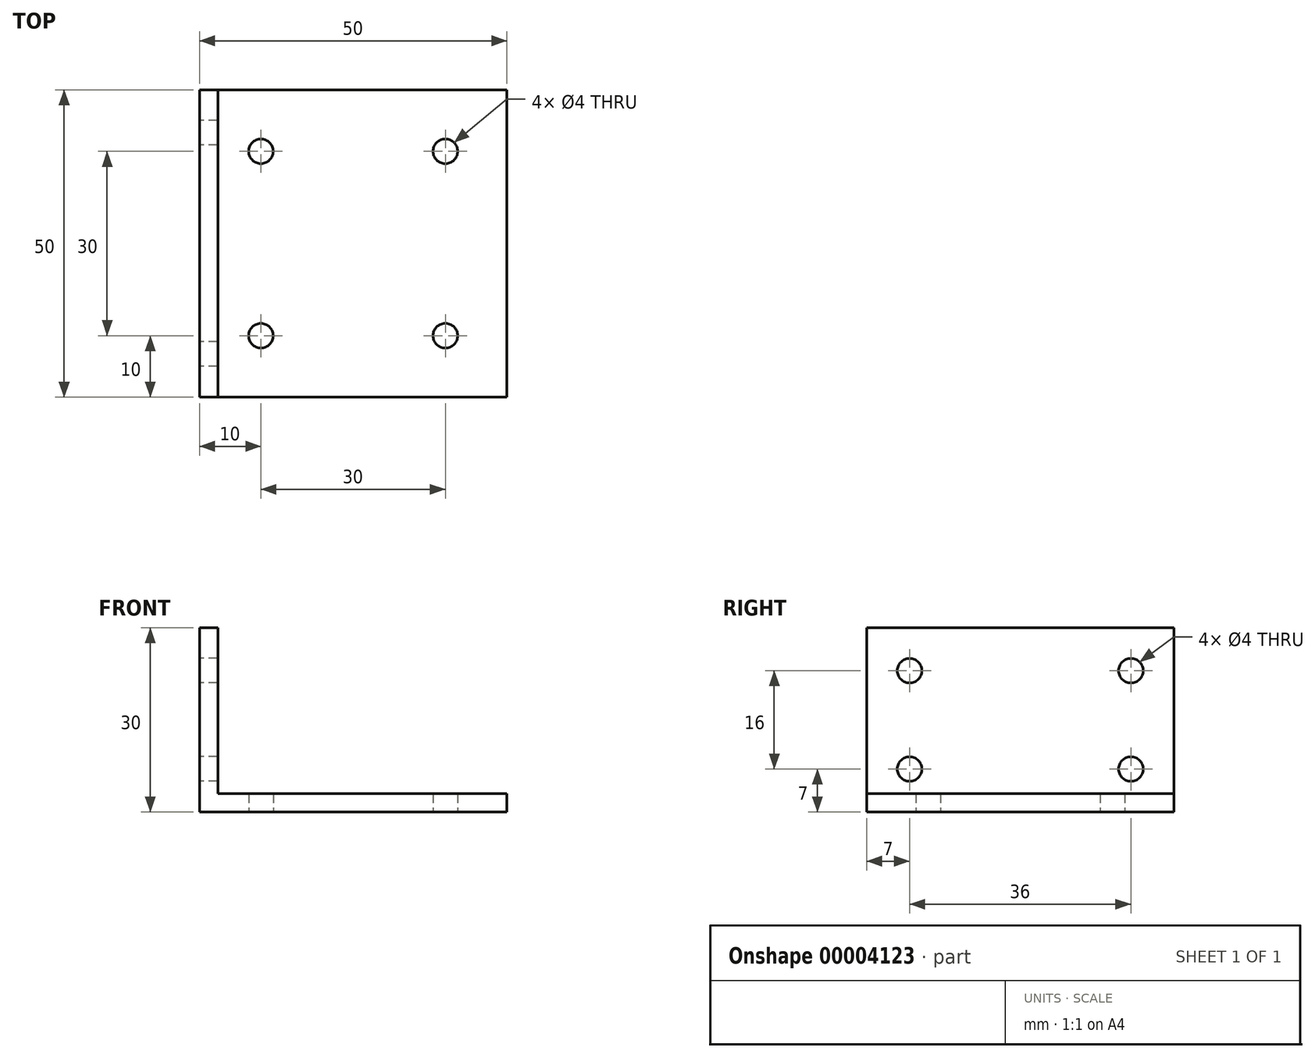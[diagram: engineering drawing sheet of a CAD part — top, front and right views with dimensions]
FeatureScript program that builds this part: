
annotation { "Feature Type Name" : "Feature", "Feature Type Description" : "" }
export const myFeature = defineFeature(function(context is Context, id is Id, definition is map)
    precondition{}
    {
        {
            var Q0;
            Q0=qCreatedBy(makeId("Front.planeOp"),FACE);
            var sketch = newSketch(context, id + "F0", { "sketchPlane" : qUnion([Q0])});
            skLineSegment(sketch, "E0", {"start": v(0, 0) * mm, "end": v(0, 30) * mm});
            skLineSegment(sketch, "E1", {"start": v(0, 30) * mm, "end": v(3, 30) * mm});
            skLineSegment(sketch, "E2", {"start": v(3, 30) * mm, "end": v(3, 3) * mm});
            skLineSegment(sketch, "E3", {"start": v(3, 3) * mm, "end": v(50, 3) * mm});
            skLineSegment(sketch, "E4", {"start": v(50, 3) * mm, "end": v(50, 0) * mm});
            skLineSegment(sketch, "E5", {"start": v(50, 0) * mm, "end": v(0, 0) * mm});
            skSolve(sketch);
        }
        {
            var Q0;
            Q0=makeQuery(id+"F0.imprint","IMPRINT",FACE,{"disambiguationData":[TD([[makeQuery(id+"F0.imprint","IMPRINT",EDGE,{"derivedFrom":sQuery(id+"F0.wireOp",EDGE,"E0")}),-1.0]])]});
            extrude(context, id + "F1", {"entities" : qUnion([Q0]), "depth" : 50 * mm});
        }
        {
            var Q0;
            Q0=makeQuery(id+"F1.opExtrude","SWEPT_FACE",FACE,{"disambiguationData":[OSD([sQuery(id+"F0.wireOp",EDGE,"E0")])]});
            var sketch = newSketch(context, id + "F2", { "sketchPlane" : qUnion([Q0])});
            skLineSegment(sketch, "E6.bottom", {"start": v(7, 23) * mm, "end": v(43, 23) * mm});
            skLineSegment(sketch, "E6.top", {"start": v(7, 7) * mm, "end": v(43, 7) * mm});
            skLineSegment(sketch, "E6.left", {"start": v(7, 23) * mm, "end": v(7, 7) * mm});
            skLineSegment(sketch, "E6.right", {"start": v(43, 23) * mm, "end": v(43, 7) * mm});
            skCircle(sketch, "E7", {"center": v(7, 23) * mm, "radius": 2 * mm});
            skCircle(sketch, "E8", {"center": v(43, 23) * mm, "radius": 2 * mm});
            skCircle(sketch, "E9", {"center": v(43, 7) * mm, "radius": 2 * mm});
            skCircle(sketch, "E10", {"center": v(7, 7) * mm, "radius": 2 * mm});
            skSolve(sketch);
        }
        {
            var Q0;
            {var subQ1=sQuery(id+"F2.wireOp",EDGE,"E6.left");var subQ3=sQuery(id+"F2.wireOp",EDGE,"E6.bottom");var subQ5=makeQuery(id+"F2.imprint","INTERSECT",VERTEX,{"derivedFrom":[subQ3,subQ1]});Q0=makeQuery(id+"F2.imprint","IMPRINT",FACE,{"disambiguationData":[TD([[makeQuery(id+"F2.imprint","IMPRINT",EDGE,{"disambiguationData":[TD([[subQ5,-1.0]])],"derivedFrom":subQ3}),1.0]])]});}
            var Q1;
            {var subQ1=sQuery(id+"F2.wireOp",EDGE,"E6.left");var subQ3=sQuery(id+"F2.wireOp",EDGE,"E6.bottom");var subQ5=makeQuery(id+"F2.imprint","INTERSECT",VERTEX,{"derivedFrom":[subQ3,subQ1]});Q1=makeQuery(id+"F2.imprint","IMPRINT",FACE,{"disambiguationData":[TD([[makeQuery(id+"F2.imprint","IMPRINT",EDGE,{"disambiguationData":[TD([[subQ5,-1.0]])],"derivedFrom":subQ3}),-1.0]])]});}
            var Q2;
            {var subQ1=sQuery(id+"F2.wireOp",EDGE,"E6.left");var subQ3=sQuery(id+"F2.wireOp",EDGE,"E6.top");var subQ5=makeQuery(id+"F2.imprint","INTERSECT",VERTEX,{"derivedFrom":[subQ3,subQ1]});Q2=makeQuery(id+"F2.imprint","IMPRINT",FACE,{"disambiguationData":[TD([[makeQuery(id+"F2.imprint","IMPRINT",EDGE,{"disambiguationData":[TD([[subQ5,-1.0]])],"derivedFrom":subQ3}),-1.0]])]});}
            var Q3;
            {var subQ1=sQuery(id+"F2.wireOp",EDGE,"E6.left");var subQ3=sQuery(id+"F2.wireOp",EDGE,"E6.top");var subQ5=makeQuery(id+"F2.imprint","INTERSECT",VERTEX,{"derivedFrom":[subQ3,subQ1]});Q3=makeQuery(id+"F2.imprint","IMPRINT",FACE,{"disambiguationData":[TD([[makeQuery(id+"F2.imprint","IMPRINT",EDGE,{"disambiguationData":[TD([[subQ5,-1.0]])],"derivedFrom":subQ3}),1.0]])]});}
            var Q4;
            {var subQ1=sQuery(id+"F2.wireOp",EDGE,"E6.right");var subQ3=sQuery(id+"F2.wireOp",EDGE,"E6.top");var subQ5=makeQuery(id+"F2.imprint","INTERSECT",VERTEX,{"derivedFrom":[subQ3,subQ1]});Q4=makeQuery(id+"F2.imprint","IMPRINT",FACE,{"disambiguationData":[TD([[makeQuery(id+"F2.imprint","IMPRINT",EDGE,{"disambiguationData":[TD([[subQ5,1.0]])],"derivedFrom":subQ3}),-1.0]])]});}
            var Q5;
            {var subQ1=sQuery(id+"F2.wireOp",EDGE,"E6.right");var subQ3=sQuery(id+"F2.wireOp",EDGE,"E6.top");var subQ5=makeQuery(id+"F2.imprint","INTERSECT",VERTEX,{"derivedFrom":[subQ3,subQ1]});Q5=makeQuery(id+"F2.imprint","IMPRINT",FACE,{"disambiguationData":[TD([[makeQuery(id+"F2.imprint","IMPRINT",EDGE,{"disambiguationData":[TD([[subQ5,1.0]])],"derivedFrom":subQ3}),1.0]])]});}
            var Q6;
            {var subQ1=sQuery(id+"F2.wireOp",EDGE,"E6.right");var subQ3=sQuery(id+"F2.wireOp",EDGE,"E6.bottom");var subQ5=makeQuery(id+"F2.imprint","INTERSECT",VERTEX,{"derivedFrom":[subQ3,subQ1]});Q6=makeQuery(id+"F2.imprint","IMPRINT",FACE,{"disambiguationData":[TD([[makeQuery(id+"F2.imprint","IMPRINT",EDGE,{"disambiguationData":[TD([[subQ5,1.0]])],"derivedFrom":subQ3}),1.0]])]});}
            var Q7;
            {var subQ1=sQuery(id+"F2.wireOp",EDGE,"E6.right");var subQ3=sQuery(id+"F2.wireOp",EDGE,"E6.bottom");var subQ5=makeQuery(id+"F2.imprint","INTERSECT",VERTEX,{"derivedFrom":[subQ3,subQ1]});Q7=makeQuery(id+"F2.imprint","IMPRINT",FACE,{"disambiguationData":[TD([[makeQuery(id+"F2.imprint","IMPRINT",EDGE,{"disambiguationData":[TD([[subQ5,1.0]])],"derivedFrom":subQ3}),-1.0]])]});}
            extrude(context, id + "F3", {"entities" : qUnion([Q0, Q1, Q2, Q3, Q4, Q5, Q6, Q7]), "operationType" : NewBodyOperationType.REMOVE, "oppositeDirection" : true, "depth" : 25 * mm});
        }
        {
            var Q0;
            Q0=makeQuery(id+"F1.opExtrude","SWEPT_FACE",FACE,{"disambiguationData":[OSD([sQuery(id+"F0.wireOp",EDGE,"E5")])]});
            var sketch = newSketch(context, id + "F4", { "sketchPlane" : qUnion([Q0])});
            skLineSegment(sketch, "E11.bottom", {"start": v(10, 40) * mm, "end": v(40, 40) * mm});
            skLineSegment(sketch, "E11.top", {"start": v(10, 10) * mm, "end": v(40, 10) * mm});
            skLineSegment(sketch, "E11.left", {"start": v(10, 40) * mm, "end": v(10, 10) * mm});
            skLineSegment(sketch, "E11.right", {"start": v(40, 40) * mm, "end": v(40, 10) * mm});
            skCircle(sketch, "E12", {"center": v(10, 40) * mm, "radius": 2 * mm});
            skCircle(sketch, "E13", {"center": v(40, 40) * mm, "radius": 2 * mm});
            skCircle(sketch, "E14", {"center": v(10, 10) * mm, "radius": 2 * mm});
            skCircle(sketch, "E15", {"center": v(40, 10) * mm, "radius": 2 * mm});
            skSolve(sketch);
        }
        {
            var Q0;
            {var subQ1=sQuery(id+"F4.wireOp",EDGE,"E11.left");var subQ3=sQuery(id+"F4.wireOp",EDGE,"E11.bottom");var subQ5=makeQuery(id+"F4.imprint","INTERSECT",VERTEX,{"derivedFrom":[subQ3,subQ1]});Q0=makeQuery(id+"F4.imprint","IMPRINT",FACE,{"disambiguationData":[TD([[makeQuery(id+"F4.imprint","IMPRINT",EDGE,{"disambiguationData":[TD([[subQ5,-1.0]])],"derivedFrom":subQ3}),1.0]])]});}
            var Q1;
            {var subQ1=sQuery(id+"F4.wireOp",EDGE,"E11.left");var subQ3=sQuery(id+"F4.wireOp",EDGE,"E11.bottom");var subQ5=makeQuery(id+"F4.imprint","INTERSECT",VERTEX,{"derivedFrom":[subQ3,subQ1]});Q1=makeQuery(id+"F4.imprint","IMPRINT",FACE,{"disambiguationData":[TD([[makeQuery(id+"F4.imprint","IMPRINT",EDGE,{"disambiguationData":[TD([[subQ5,-1.0]])],"derivedFrom":subQ3}),-1.0]])]});}
            var Q2;
            {var subQ1=sQuery(id+"F4.wireOp",EDGE,"E11.left");var subQ3=sQuery(id+"F4.wireOp",EDGE,"E11.top");var subQ5=makeQuery(id+"F4.imprint","INTERSECT",VERTEX,{"derivedFrom":[subQ3,subQ1]});Q2=makeQuery(id+"F4.imprint","IMPRINT",FACE,{"disambiguationData":[TD([[makeQuery(id+"F4.imprint","IMPRINT",EDGE,{"disambiguationData":[TD([[subQ5,-1.0]])],"derivedFrom":subQ3}),-1.0]])]});}
            var Q3;
            {var subQ1=sQuery(id+"F4.wireOp",EDGE,"E11.left");var subQ3=sQuery(id+"F4.wireOp",EDGE,"E11.top");var subQ5=makeQuery(id+"F4.imprint","INTERSECT",VERTEX,{"derivedFrom":[subQ3,subQ1]});Q3=makeQuery(id+"F4.imprint","IMPRINT",FACE,{"disambiguationData":[TD([[makeQuery(id+"F4.imprint","IMPRINT",EDGE,{"disambiguationData":[TD([[subQ5,-1.0]])],"derivedFrom":subQ3}),1.0]])]});}
            var Q4;
            {var subQ1=sQuery(id+"F4.wireOp",EDGE,"E11.right");var subQ3=sQuery(id+"F4.wireOp",EDGE,"E11.top");var subQ5=makeQuery(id+"F4.imprint","INTERSECT",VERTEX,{"derivedFrom":[subQ3,subQ1]});Q4=makeQuery(id+"F4.imprint","IMPRINT",FACE,{"disambiguationData":[TD([[makeQuery(id+"F4.imprint","IMPRINT",EDGE,{"disambiguationData":[TD([[subQ5,1.0]])],"derivedFrom":subQ3}),-1.0]])]});}
            var Q5;
            {var subQ0=sQuery(id+"F4.wireOp",EDGE,"E11.right");var subQ3=sQuery(id+"F4.wireOp",EDGE,"E11.top");var subQ4=makeQuery(id+"F4.imprint","INTERSECT",VERTEX,{"derivedFrom":[subQ3,subQ0]});Q5=makeQuery(id+"F4.imprint","IMPRINT",FACE,{"disambiguationData":[TD([[makeQuery(id+"F4.imprint","IMPRINT",EDGE,{"disambiguationData":[TD([[subQ4,1.0]])],"derivedFrom":subQ3}),1.0]])]});}
            var Q6;
            {var subQ1=sQuery(id+"F4.wireOp",EDGE,"E11.right");var subQ3=sQuery(id+"F4.wireOp",EDGE,"E11.bottom");var subQ5=makeQuery(id+"F4.imprint","INTERSECT",VERTEX,{"derivedFrom":[subQ3,subQ1]});Q6=makeQuery(id+"F4.imprint","IMPRINT",FACE,{"disambiguationData":[TD([[makeQuery(id+"F4.imprint","IMPRINT",EDGE,{"disambiguationData":[TD([[subQ5,1.0]])],"derivedFrom":subQ3}),-1.0]])]});}
            var Q7;
            {var subQ1=sQuery(id+"F4.wireOp",EDGE,"E11.right");var subQ3=sQuery(id+"F4.wireOp",EDGE,"E11.bottom");var subQ5=makeQuery(id+"F4.imprint","INTERSECT",VERTEX,{"derivedFrom":[subQ3,subQ1]});Q7=makeQuery(id+"F4.imprint","IMPRINT",FACE,{"disambiguationData":[TD([[makeQuery(id+"F4.imprint","IMPRINT",EDGE,{"disambiguationData":[TD([[subQ5,1.0]])],"derivedFrom":subQ3}),1.0]])]});}
            extrude(context, id + "F5", {"entities" : qUnion([Q0, Q1, Q2, Q3, Q4, Q5, Q6, Q7]), "operationType" : NewBodyOperationType.REMOVE, "oppositeDirection" : true, "depth" : 25 * mm});
        }
    });
